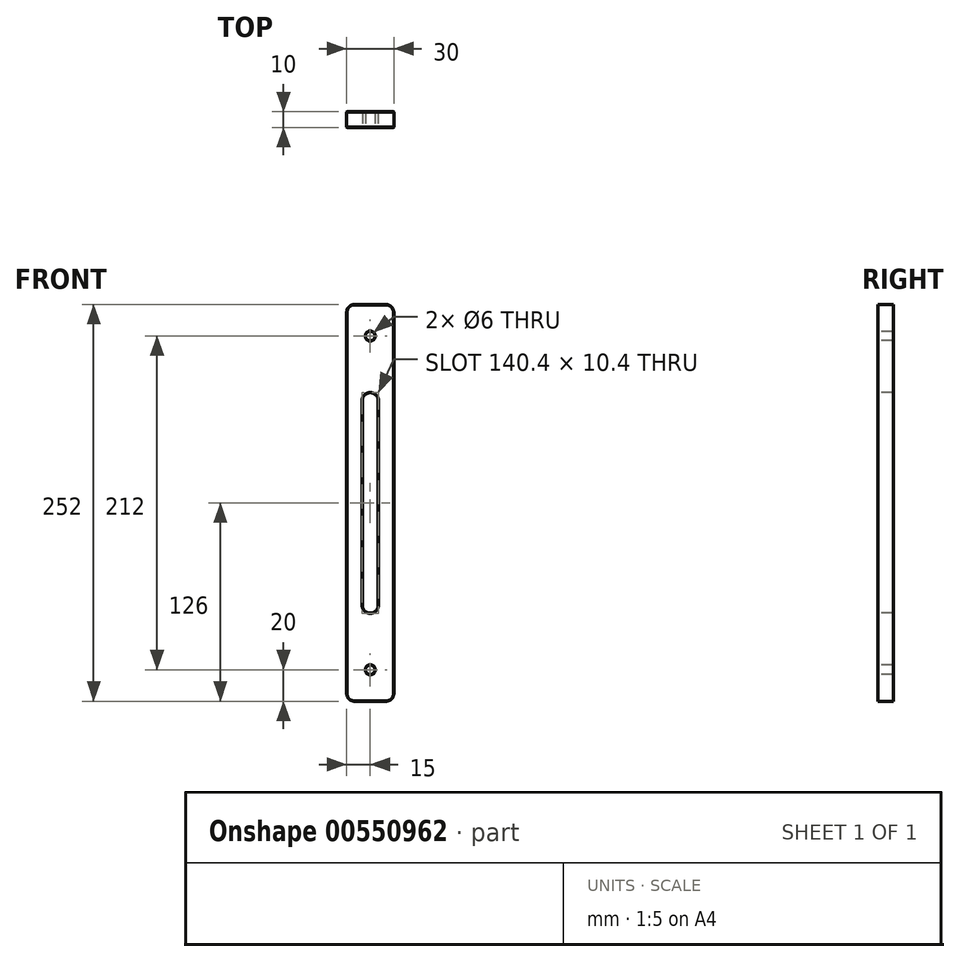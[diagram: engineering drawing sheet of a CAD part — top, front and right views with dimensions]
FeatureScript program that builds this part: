
annotation { "Feature Type Name" : "Feature", "Feature Type Description" : "" }
export const myFeature = defineFeature(function(context is Context, id is Id, definition is map)
    precondition{}
    {
        {
            var Q0;
            Q0=qCreatedBy(makeId("Front.planeOp"),FACE);
            var sketch = newSketch(context, id + "F0", { "sketchPlane" : qUnion([Q0])});
            skLineSegment(sketch, "E0", {"start": v(0, 0) * mm, "end": v(0, 252) * mm});
            skLineSegment(sketch, "E1", {"start": v(0, 0) * mm, "end": v(30, 0) * mm});
            skLineSegment(sketch, "E2", {"start": v(30, 0) * mm, "end": v(30, 252) * mm});
            skLineSegment(sketch, "E3", {"start": v(30, 252) * mm, "end": v(0, 252) * mm});
            skSolve(sketch);
        }
        {
            var Q0;
            Q0=makeQuery(id+"F0.imprint","IMPRINT",FACE,{"disambiguationData":[TD([[makeQuery(id+"F0.imprint","IMPRINT",EDGE,{"derivedFrom":sQuery(id+"F0.wireOp",EDGE,"E0")}),-1.0]])]});
            extrude(context, id + "F1", {"entities" : qUnion([Q0]), "depth" : 10 * mm, "offsetDistance" : 25 * mm});
        }
        {
            var Q0;
            Q0=makeQuery(id+"F1.opExtrude","SWEPT_EDGE",EDGE,{"disambiguationData":[OSD([sQuery(id+"F0.wireOp",EDGE,"E2"),sQuery(id+"F0.wireOp",EDGE,"E3")])]});
            var Q1;
            Q1=makeQuery(id+"F1.opExtrude","SWEPT_EDGE",EDGE,{"disambiguationData":[OSD([sQuery(id+"F0.wireOp",EDGE,"E0"),sQuery(id+"F0.wireOp",EDGE,"E3")])]});
            var Q2;
            Q2=makeQuery(id+"F1.opExtrude","SWEPT_EDGE",EDGE,{"disambiguationData":[OSD([sQuery(id+"F0.wireOp",EDGE,"E1"),sQuery(id+"F0.wireOp",EDGE,"E2")])]});
            var Q3;
            Q3=makeQuery(id+"F1.opExtrude","SWEPT_EDGE",EDGE,{"disambiguationData":[OSD([sQuery(id+"F0.wireOp",EDGE,"E0"),sQuery(id+"F0.wireOp",EDGE,"E1")])]});
            fillet(context, id + "F2", {"entities" : qUnion([Q0, Q1, Q2, Q3]), "radius" : 5 * mm, "tangentPropagation" : true, "allowEdgeOverflow" : false});
        }
        {
            var Q0;
            Q0=makeQuery(id+"F1.opExtrude","CAP_FACE",FACE,{"disambiguationData":[OSD([sQuery(id+"F0.wireOp",EDGE,"E0"),sQuery(id+"F0.wireOp",EDGE,"E1"),sQuery(id+"F0.wireOp",EDGE,"E2"),sQuery(id+"F0.wireOp",EDGE,"E3")])],"isStart":false});
            var sketch = newSketch(context, id + "F3", { "sketchPlane" : qUnion([Q0])});
            skPoint(sketch, "E4.endSnap0", {"position": v(15, 126) * mm});
            skLineSegment(sketch, "E5.0", {"start": v(10, 126) * mm, "end": v(10, 56) * mm});
            skLineSegment(sketch, "E5.1", {"start": v(10, 126) * mm, "end": v(10, 196) * mm});
            skLineSegment(sketch, "E6.0", {"start": v(20, 126) * mm, "end": v(20, 56) * mm});
            skLineSegment(sketch, "E6.1", {"start": v(20, 126) * mm, "end": v(20, 196) * mm});
            skLineSegment(sketch, "E7", {"start": v(10, 56) * mm, "end": v(20, 56) * mm});
            skLineSegment(sketch, "E8", {"start": v(10, 196) * mm, "end": v(20, 196) * mm});
            skPoint(sketch, "E9.end.orphan", {"position": v(15, 196) * mm});
            skPoint(sketch, "E4.end.orphan", {"position": v(15, 56) * mm});
            skPoint(sketch, "E10.start.orphan", {"position": v(0, 126) * mm});
            skPoint(sketch, "E11.trimOffspring.end.orphan", {"position": v(30, 126) * mm});
            skSolve(sketch);
        }
        {
            var Q0;
            Q0=makeQuery(id+"F3.imprint","IMPRINT",FACE,{"disambiguationData":[TD([[makeQuery(id+"F3.imprint","IMPRINT",EDGE,{"derivedFrom":sQuery(id+"F3.wireOp",EDGE,"E5.1")}),-1.0]])]});
            extrude(context, id + "F4", {"entities" : qUnion([Q0]), "operationType" : NewBodyOperationType.REMOVE, "oppositeDirection" : true, "depth" : 25 * mm, "offsetDistance" : 25 * mm});
        }
        {
            var Q0;
            Q0=makeQuery(id+"F4.boolean.opBoolean","COPY",EDGE,{"derivedFrom":makeQuery(id+"F4.opExtrude","SWEPT_EDGE",EDGE,{"disambiguationData":[OSD([sQuery(id+"F3.wireOp",EDGE,"E5.1"),sQuery(id+"F3.wireOp",EDGE,"E8")])]})});
            var Q1;
            Q1=makeQuery(id+"F4.boolean.opBoolean","COPY",EDGE,{"derivedFrom":makeQuery(id+"F4.opExtrude","SWEPT_EDGE",EDGE,{"disambiguationData":[OSD([sQuery(id+"F3.wireOp",EDGE,"E6.1"),sQuery(id+"F3.wireOp",EDGE,"E8")])]})});
            var Q2;
            Q2=makeQuery(id+"F4.boolean.opBoolean","COPY",EDGE,{"derivedFrom":makeQuery(id+"F4.opExtrude","SWEPT_EDGE",EDGE,{"disambiguationData":[OSD([sQuery(id+"F3.wireOp",EDGE,"E6.0"),sQuery(id+"F3.wireOp",EDGE,"E7")])]})});
            var Q3;
            Q3=makeQuery(id+"F4.boolean.opBoolean","COPY",EDGE,{"derivedFrom":makeQuery(id+"F4.opExtrude","SWEPT_EDGE",EDGE,{"disambiguationData":[OSD([sQuery(id+"F3.wireOp",EDGE,"E5.0"),sQuery(id+"F3.wireOp",EDGE,"E7")])]})});
            fillet(context, id + "F5", {"entities" : qUnion([Q0, Q1, Q2, Q3]), "radius" : 5 * mm, "tangentPropagation" : true, "allowEdgeOverflow" : false});
        }
        {
            var Q0;
            Q0=makeQuery(id+"F1.opExtrude","CAP_FACE",FACE,{"disambiguationData":[OSD([sQuery(id+"F0.wireOp",EDGE,"E0"),sQuery(id+"F0.wireOp",EDGE,"E1"),sQuery(id+"F0.wireOp",EDGE,"E2"),sQuery(id+"F0.wireOp",EDGE,"E3")])],"isStart":false});
            var sketch = newSketch(context, id + "F6", { "sketchPlane" : qUnion([Q0])});
            skCircle(sketch, "E12", {"center": v(15, 232) * mm, "radius": 3 * mm});
            skPoint(sketch, "E13.orphan", {"position": v(15, 252) * mm});
            skSolve(sketch);
        }
        {
            var Q0;
            Q0=makeQuery(id+"F6.imprint","IMPRINT",FACE,{"disambiguationData":[TD([[makeQuery(id+"F6.imprint","IMPRINT",EDGE,{"derivedFrom":sQuery(id+"F6.wireOp",EDGE,"E12")}),1.0]])]});
            extrude(context, id + "F7", {"entities" : qUnion([Q0]), "operationType" : NewBodyOperationType.REMOVE, "oppositeDirection" : true, "depth" : 25 * mm, "offsetDistance" : 25 * mm});
        }
        {
            var Q0;
            Q0=makeQuery(id+"F1.opExtrude","CAP_FACE",FACE,{"disambiguationData":[OSD([sQuery(id+"F0.wireOp",EDGE,"E0"),sQuery(id+"F0.wireOp",EDGE,"E1"),sQuery(id+"F0.wireOp",EDGE,"E2"),sQuery(id+"F0.wireOp",EDGE,"E3")])],"isStart":false});
            var sketch = newSketch(context, id + "F8", { "sketchPlane" : qUnion([Q0])});
            skPoint(sketch, "E14.endSnap0", {"position": v(15, 0) * mm});
            skCircle(sketch, "E15", {"center": v(15, 20) * mm, "radius": 3 * mm});
            skSolve(sketch);
        }
        {
            var Q0;
            Q0=makeQuery(id+"F8.imprint","IMPRINT",FACE,{"disambiguationData":[TD([[makeQuery(id+"F8.imprint","IMPRINT",EDGE,{"derivedFrom":sQuery(id+"F8.wireOp",EDGE,"E15")}),1.0]])]});
            extrude(context, id + "F9", {"entities" : qUnion([Q0]), "operationType" : NewBodyOperationType.REMOVE, "oppositeDirection" : true, "depth" : 25 * mm, "offsetDistance" : 25 * mm});
        }
        {
            var Q0;
            Q0=makeQuery(id+"F1.opExtrude","CAP_FACE",FACE,{"disambiguationData":[OSD([sQuery(id+"F0.wireOp",EDGE,"E0"),sQuery(id+"F0.wireOp",EDGE,"E1"),sQuery(id+"F0.wireOp",EDGE,"E2"),sQuery(id+"F0.wireOp",EDGE,"E3")])],"isStart":false});
            chamfer(context, id + "F10", {"entities" : qUnion([Q0]), "width" : .2 * mm, "tangentPropagation" : true});
        }
        {
            var Q0;
            Q0=makeQuery(id+"F1.opExtrude","CAP_FACE",FACE,{"disambiguationData":[OSD([sQuery(id+"F0.wireOp",EDGE,"E0"),sQuery(id+"F0.wireOp",EDGE,"E1"),sQuery(id+"F0.wireOp",EDGE,"E2"),sQuery(id+"F0.wireOp",EDGE,"E3")])],"isStart":true});
            chamfer(context, id + "F11", {"entities" : qUnion([Q0]), "width" : .2 * mm, "tangentPropagation" : true});
        }
    });
